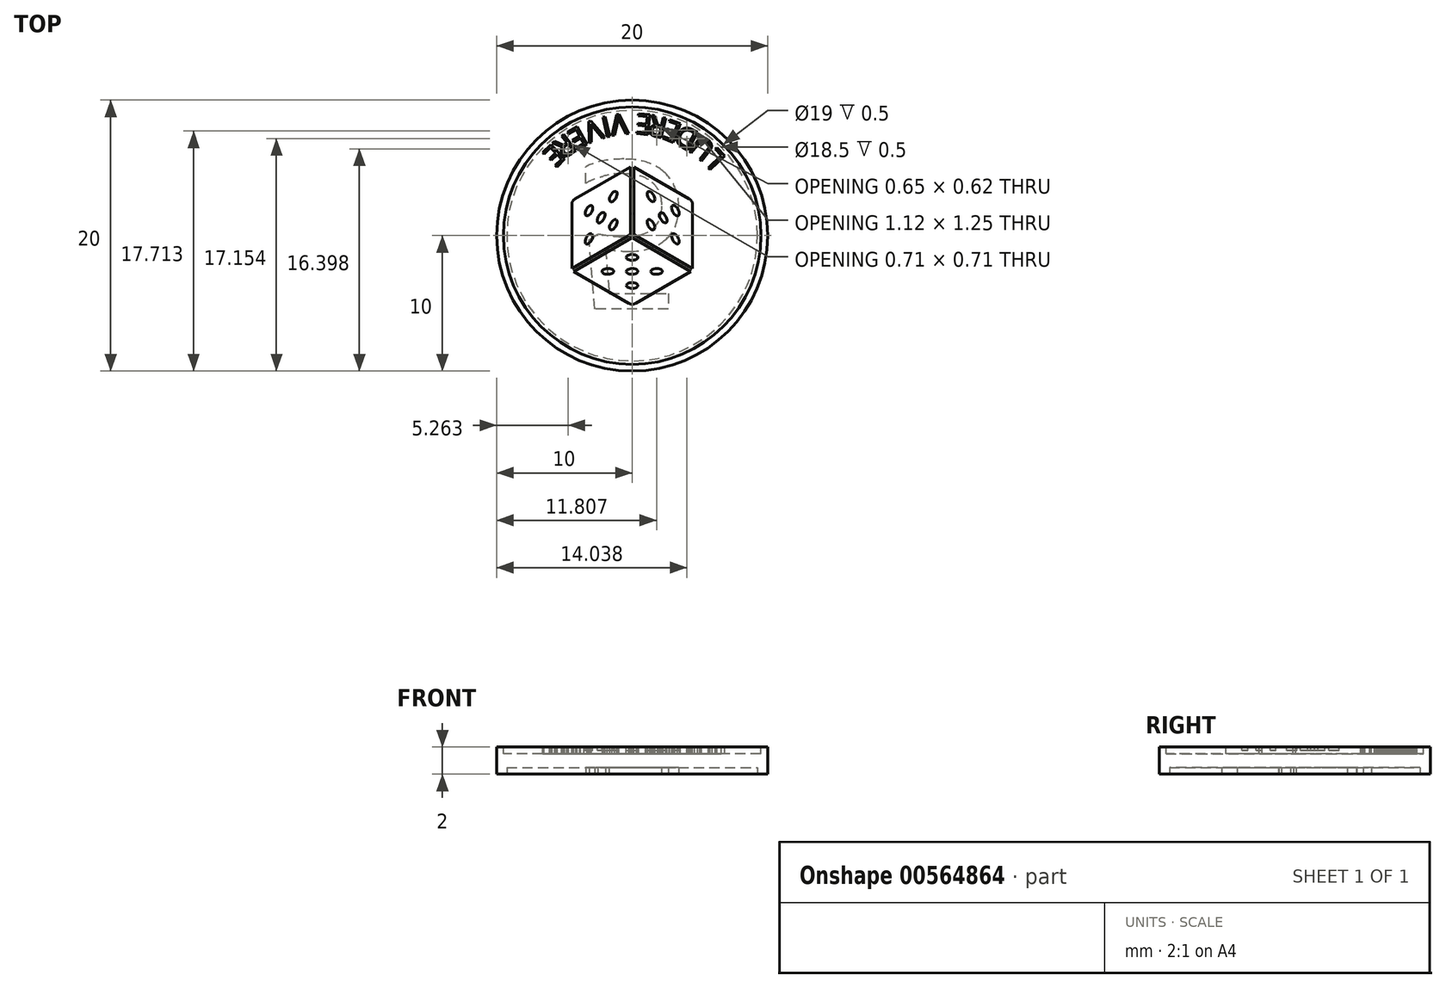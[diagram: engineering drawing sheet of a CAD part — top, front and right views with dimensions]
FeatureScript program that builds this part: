
annotation { "Feature Type Name" : "Feature", "Feature Type Description" : "" }
export const myFeature = defineFeature(function(context is Context, id is Id, definition is map)
    precondition{}
    {
        {
            var Q0;
            Q0=qCreatedBy(makeId("Top.planeOp"),FACE);
            var sketch = newSketch(context, id + "F0", { "sketchPlane" : qUnion([Q0])});
            skCircle(sketch, "E0", {"center": v(0, 0) * mm, "radius": 10 * mm});
            skSolve(sketch);
        }
        {
            var Q0;
            Q0=qSketchRegion(id+"F0",true);
            extrude(context, id + "F1", {"entities" : qUnion([Q0]), "depth" : 2 * mm});
        }
        {
            var Q0;
            Q0=makeQuery(id+"F1.opExtrude","CAP_FACE",FACE,{"disambiguationData":[OSD([sQuery(id+"F0.wireOp",EDGE,"E0")])],"isStart":false});
            var sketch = newSketch(context, id + "F2", { "sketchPlane" : qUnion([Q0])});
            skCircle(sketch, "E1.0", {"center": v(0, 0) * mm, "radius": 9.5 * mm});
            skSolve(sketch);
        }
        {
            var Q0;
            Q0=qSketchRegion(id+"F2",true);
            extrude(context, id + "F3", {"entities" : qUnion([Q0]), "operationType" : NewBodyOperationType.REMOVE, "oppositeDirection" : true, "depth" : 0.5 * mm});
        }
        {
            var Q0;
            Q0=makeQuery(id+"F1.opExtrude","CAP_FACE",FACE,{"disambiguationData":[OSD([sQuery(id+"F0.wireOp",EDGE,"E0")])],"isStart":true});
            var sketch = newSketch(context, id + "F4", { "sketchPlane" : qUnion([Q0])});
            skCircle(sketch, "E2.0", {"center": v(0, 0) * mm, "radius": 9.25 * mm});
            skSolve(sketch);
        }
        {
            var Q0;
            Q0=qSketchRegion(id+"F4",true);
            extrude(context, id + "F5", {"entities" : qUnion([Q0]), "operationType" : NewBodyOperationType.REMOVE, "oppositeDirection" : true, "depth" : 0.5 * mm});
        }
        {
            var Q0;
            Q0=makeQuery(id+"F2.imprint","IMPRINT",FACE,{"disambiguationData":[TD([[makeQuery(id+"F2.imprint","IMPRINT",EDGE,{"derivedFrom":sQuery(id+"F2.wireOp",EDGE,"E1.0")}),1.0]])]});
            var sketch = newSketch(context, id + "F6", { "sketchPlane" : qUnion([Q0])});
            skLineSegment(sketch, "E3", {"start": v(0, 0) * mm, "end": v(0, 9.5) * mm, "construction": true});
            skLineSegment(sketch, "E4", {"start": v(0, 0) * mm, "end": v(-8.23, -4.75) * mm, "construction": true});
            skLineSegment(sketch, "E5", {"start": v(0, 0) * mm, "end": v(8.23, -4.75) * mm, "construction": true});
            skCircle(sketch, "E6", {"center": v(0, 0) * mm, "radius": 9.5 * mm, "construction": true});
            skLineSegment(sketch, "E7", {"start": v(-0.13, 5.07) * mm, "end": v(-0.12, 0.07) * mm});
            skLineSegment(sketch, "E8", {"start": v(-0.12, 0.07) * mm, "end": v(-4.46, -2.43) * mm});
            skLineSegment(sketch, "E9", {"start": v(-4.46, -2.43) * mm, "end": v(-4.46, 2.28) * mm});
            skLineSegment(sketch, "E10", {"start": v(-4.2, 2.72) * mm, "end": v(-0.13, 5.07) * mm});
            skPoint(sketch, "E11.visualSharp", {"position": v(-4.46, 2.57) * mm});
            skArc(sketch, "E11.filletArc", {"start": v(-4.2, 2.72) * mm, "mid": v(-4.39, 2.53) * mm, "end": v(-4.46, 2.28) * mm});
            skPoint(sketch, "E12.1.1", {"position": v(0, -5.14) * mm});
            skLineSegment(sketch, "E12.1.3", {"start": v(-4.33, -2.64) * mm, "end": v(0, -0.14) * mm});
            skLineSegment(sketch, "E12.1.5", {"start": v(0, -0.14) * mm, "end": v(4.33, -2.64) * mm});
            skLineSegment(sketch, "E12.1.6", {"start": v(4.33, -2.64) * mm, "end": v(0.25, -5) * mm});
            skLineSegment(sketch, "E12.1.7", {"start": v(-0.25, -5) * mm, "end": v(-4.33, -2.64) * mm});
            skArc(sketch, "E12.1.8", {"start": v(-0.25, -5) * mm, "mid": v(0, -5.07) * mm, "end": v(0.25, -5) * mm});
            skPoint(sketch, "E12.2.1", {"position": v(4.46, 2.57) * mm});
            skLineSegment(sketch, "E12.2.3", {"start": v(4.46, -2.43) * mm, "end": v(0.13, 0.07) * mm});
            skLineSegment(sketch, "E12.2.5", {"start": v(0.12, 0.07) * mm, "end": v(0.13, 5.07) * mm});
            skLineSegment(sketch, "E12.2.6", {"start": v(0.13, 5.07) * mm, "end": v(4.2, 2.72) * mm});
            skLineSegment(sketch, "E12.2.7", {"start": v(4.46, 2.28) * mm, "end": v(4.46, -2.43) * mm});
            skArc(sketch, "E12.2.8", {"start": v(4.46, 2.28) * mm, "mid": v(4.39, 2.53) * mm, "end": v(4.2, 2.72) * mm});
            skSolve(sketch);
        }
        {
            var Q0;
            Q0=qSketchRegion(id+"F6",true);
            extrude(context, id + "F7", {"entities" : qUnion([Q0]), "operationType" : NewBodyOperationType.ADD, "endBound" : BoundingType.UP_TO_NEXT, "oppositeDirection" : true, "depth" : 25 * mm});
        }
        {
            var Q0;
            Q0=makeQuery(id+"F7.opExtrude","CAP_FACE",FACE,{"disambiguationData":[OSD([sQuery(id+"F6.wireOp",EDGE,"E12.1.3"),sQuery(id+"F6.wireOp",EDGE,"E12.1.5"),sQuery(id+"F6.wireOp",EDGE,"E12.1.6"),sQuery(id+"F6.wireOp",EDGE,"E12.1.7"),sQuery(id+"F6.wireOp",EDGE,"E12.1.8")])],"isStart":true});
            var sketch = newSketch(context, id + "F8", { "sketchPlane" : qUnion([Q0])});
            skLineSegment(sketch, "E13", {"start": v(-4.33, -2.64) * mm, "end": v(4.33, -2.64) * mm, "construction": true});
            skLineSegment(sketch, "E14", {"start": v(0, -0.14) * mm, "end": v(0, -5.07) * mm, "construction": true});
            skLineSegment(sketch, "E15", {"start": v(-0.56, -2.64) * mm, "end": v(0, -2.32) * mm, "construction": true});
            skLineSegment(sketch, "E16", {"start": v(0, -2.32) * mm, "end": v(0.56, -2.64) * mm, "construction": true});
            skLineSegment(sketch, "E17", {"start": v(0.56, -2.64) * mm, "end": v(0, -2.97) * mm, "construction": true});
            skLineSegment(sketch, "E18", {"start": v(0, -2.97) * mm, "end": v(-0.56, -2.64) * mm, "construction": true});
            skLineSegment(sketch, "E19", {"start": v(-0.28, -2.48) * mm, "end": v(0.28, -2.8) * mm, "construction": true});
            skLineSegment(sketch, "E20", {"start": v(-0.28, -2.8) * mm, "end": v(0.28, -2.48) * mm, "construction": true});
            skEllipse(sketch, "E21", {"center": v(0, -2.64) * mm, "majorRadius": 0.43 * mm, "minorRadius": 0.22 * mm, "majorAxis": v(-1, 0)});
            skEllipse(sketch, "E22.1.0.0", {"center": v(1.8, -2.64) * mm, "majorRadius": 0.43 * mm, "minorRadius": 0.22 * mm, "majorAxis": v(-1, 0)});
            skLineSegment(sketch, "E22.direction1", {"start": v(0, -2.64) * mm, "end": v(1.8, -2.64) * mm, "construction": true});
            skEllipse(sketch, "E23.1.0.0", {"center": v(-1.8, -2.64) * mm, "majorRadius": 0.43 * mm, "minorRadius": 0.22 * mm, "majorAxis": v(-1, 0)});
            skLineSegment(sketch, "E23.direction1", {"start": v(0, -2.64) * mm, "end": v(-1.8, -2.64) * mm, "construction": true});
            skEllipse(sketch, "E24.1.0.0", {"center": v(0, -3.68) * mm, "majorRadius": 0.43 * mm, "minorRadius": 0.22 * mm, "majorAxis": v(-1, 0)});
            skLineSegment(sketch, "E24.direction1", {"start": v(0, -2.64) * mm, "end": v(0, -3.68) * mm, "construction": true});
            skLineSegment(sketch, "E25", {"start": v(0, -3.68) * mm, "end": v(1.8, -2.64) * mm, "construction": true});
            skEllipse(sketch, "E26.1.0.0", {"center": v(0, -1.6) * mm, "majorRadius": 0.43 * mm, "minorRadius": 0.22 * mm, "majorAxis": v(-1, 0)});
            skLineSegment(sketch, "E26.direction1", {"start": v(0, -2.64) * mm, "end": v(0, -1.6) * mm, "construction": true});
            skLineSegment(sketch, "E27", {"start": v(-1.8, -2.64) * mm, "end": v(0, -1.6) * mm});
            skLineSegment(sketch, "E28.1.0", {"start": v(2.3, 1.32) * mm, "end": v(3.2, -0.24) * mm, "construction": true});
            skLineSegment(sketch, "E28.1.1", {"start": v(3.2, -0.24) * mm, "end": v(1.4, 0.8) * mm});
            skEllipse(sketch, "E28.1.2", {"center": v(1.4, 0.8) * mm, "majorRadius": 0.43 * mm, "minorRadius": 0.22 * mm, "majorAxis": v(0.5, -0.87)});
            skEllipse(sketch, "E28.1.3", {"center": v(1.4, 2.88) * mm, "majorRadius": 0.43 * mm, "minorRadius": 0.22 * mm, "majorAxis": v(0.5, -0.87)});
            skLineSegment(sketch, "E28.1.4", {"start": v(2.3, 1.32) * mm, "end": v(1.4, 2.88) * mm, "construction": true});
            skEllipse(sketch, "E28.1.5", {"center": v(3.2, -0.24) * mm, "majorRadius": 0.43 * mm, "minorRadius": 0.22 * mm, "majorAxis": v(0.5, -0.87)});
            skLineSegment(sketch, "E28.1.6", {"start": v(2.3, 1.32) * mm, "end": v(1.4, 0.8) * mm, "construction": true});
            skEllipse(sketch, "E28.1.7", {"center": v(3.2, 1.84) * mm, "majorRadius": 0.43 * mm, "minorRadius": 0.22 * mm, "majorAxis": v(0.5, -0.87)});
            skLineSegment(sketch, "E28.1.8", {"start": v(4.46, -2.43) * mm, "end": v(0.12, 5.07) * mm, "construction": true});
            skLineSegment(sketch, "E28.1.9", {"start": v(0.12, 0.07) * mm, "end": v(4.39, 2.53) * mm, "construction": true});
            skLineSegment(sketch, "E28.1.10", {"start": v(3.2, 1.84) * mm, "end": v(1.4, 2.88) * mm, "construction": true});
            skLineSegment(sketch, "E28.1.11", {"start": v(2.3, 1.32) * mm, "end": v(3.2, 1.84) * mm, "construction": true});
            skEllipse(sketch, "E28.1.12", {"center": v(2.3, 1.32) * mm, "majorRadius": 0.43 * mm, "minorRadius": 0.22 * mm, "majorAxis": v(0.5, -0.87)});
            skLineSegment(sketch, "E28.1.13", {"start": v(2.57, 1.16) * mm, "end": v(2, 1.48) * mm, "construction": true});
            skLineSegment(sketch, "E28.1.14", {"start": v(2.3, 1) * mm, "end": v(2.3, 1.65) * mm, "construction": true});
            skLineSegment(sketch, "E28.1.15", {"start": v(2, 1.8) * mm, "end": v(2.57, 1.48) * mm, "construction": true});
            skLineSegment(sketch, "E28.1.16", {"start": v(2.57, 1.48) * mm, "end": v(2.57, 0.83) * mm, "construction": true});
            skLineSegment(sketch, "E28.1.17", {"start": v(2, 1.16) * mm, "end": v(2, 1.8) * mm, "construction": true});
            skLineSegment(sketch, "E28.1.18", {"start": v(2.57, 0.83) * mm, "end": v(2, 1.16) * mm, "construction": true});
            skLineSegment(sketch, "E28.2.0", {"start": v(-2.3, 1.32) * mm, "end": v(-1.4, 2.88) * mm, "construction": true});
            skLineSegment(sketch, "E28.2.1", {"start": v(-1.4, 2.88) * mm, "end": v(-1.4, 0.8) * mm});
            skEllipse(sketch, "E28.2.2", {"center": v(-1.4, 0.8) * mm, "majorRadius": 0.43 * mm, "minorRadius": 0.22 * mm, "majorAxis": v(0.5, 0.87)});
            skEllipse(sketch, "E28.2.3", {"center": v(-3.2, -0.24) * mm, "majorRadius": 0.43 * mm, "minorRadius": 0.22 * mm, "majorAxis": v(0.5, 0.87)});
            skLineSegment(sketch, "E28.2.4", {"start": v(-2.3, 1.32) * mm, "end": v(-3.2, -0.24) * mm, "construction": true});
            skEllipse(sketch, "E28.2.5", {"center": v(-1.4, 2.88) * mm, "majorRadius": 0.43 * mm, "minorRadius": 0.22 * mm, "majorAxis": v(0.5, 0.87)});
            skLineSegment(sketch, "E28.2.6", {"start": v(-2.3, 1.32) * mm, "end": v(-1.4, 0.8) * mm, "construction": true});
            skEllipse(sketch, "E28.2.7", {"center": v(-3.2, 1.84) * mm, "majorRadius": 0.43 * mm, "minorRadius": 0.22 * mm, "majorAxis": v(0.5, 0.87)});
            skLineSegment(sketch, "E28.2.8", {"start": v(-0.12, 5.07) * mm, "end": v(-4.46, -2.43) * mm, "construction": true});
            skLineSegment(sketch, "E28.2.9", {"start": v(-0.12, 0.07) * mm, "end": v(-4.39, 2.53) * mm, "construction": true});
            skLineSegment(sketch, "E28.2.10", {"start": v(-3.2, 1.84) * mm, "end": v(-3.2, -0.24) * mm, "construction": true});
            skLineSegment(sketch, "E28.2.11", {"start": v(-2.3, 1.32) * mm, "end": v(-3.2, 1.84) * mm, "construction": true});
            skEllipse(sketch, "E28.2.12", {"center": v(-2.3, 1.32) * mm, "majorRadius": 0.43 * mm, "minorRadius": 0.22 * mm, "majorAxis": v(0.5, 0.87)});
            skLineSegment(sketch, "E28.2.13", {"start": v(-2.3, 1.65) * mm, "end": v(-2.3, 1) * mm, "construction": true});
            skLineSegment(sketch, "E28.2.14", {"start": v(-2, 1.48) * mm, "end": v(-2.57, 1.16) * mm, "construction": true});
            skLineSegment(sketch, "E28.2.15", {"start": v(-2.57, 0.83) * mm, "end": v(-2.57, 1.48) * mm, "construction": true});
            skLineSegment(sketch, "E28.2.16", {"start": v(-2.57, 1.48) * mm, "end": v(-2, 1.8) * mm, "construction": true});
            skLineSegment(sketch, "E28.2.17", {"start": v(-2, 1.16) * mm, "end": v(-2.57, 0.83) * mm, "construction": true});
            skLineSegment(sketch, "E28.2.18", {"start": v(-2, 1.8) * mm, "end": v(-2, 1.16) * mm, "construction": true});
            skPoint(sketch, "E28.center", {"position": v(0, 0) * mm});
            skCircle(sketch, "E29", {"center": v(0, 0) * mm, "radius": 9 * mm, "construction": true});
            skSolve(sketch);
        }
        {
            var Q0;
            Q0=qSketchRegion(id+"F8",true);
            extrude(context, id + "F9", {"entities" : qUnion([Q0]), "operationType" : NewBodyOperationType.REMOVE, "oppositeDirection" : true, "depth" : 0.25 * mm});
        }
        {
            var Q0;
            Q0=makeQuery(id+"F7.opExtrude","CAP_FACE",FACE,{"disambiguationData":[OSD([sQuery(id+"F6.wireOp",EDGE,"E12.2.3"),sQuery(id+"F6.wireOp",EDGE,"E12.2.5"),sQuery(id+"F6.wireOp",EDGE,"E12.2.6"),sQuery(id+"F6.wireOp",EDGE,"E12.2.7"),sQuery(id+"F6.wireOp",EDGE,"E12.2.8")])],"isStart":true});
            var sketch = newSketch(context, id + "F10", { "sketchPlane" : qUnion([Q0])});
            skCircle(sketch, "E30", {"center": v(0, 0) * mm, "radius": 9 * mm, "construction": true});
            skLineSegment(sketch, "E31", {"start": v(0, 0) * mm, "end": v(0.12, 9) * mm, "construction": true});
            skText(sketch, "E32", { "text": "E", "fontName": "OpenSans-Regular.ttf"});
            skText(sketch, "E33", { "text": "L", "fontName": "OpenSans-Regular.ttf"});
            skText(sketch, "E34", { "text": "U", "fontName": "OpenSans-Regular.ttf"});
            skText(sketch, "E35", { "text": "D", "fontName": "OpenSans-Regular.ttf"});
            skText(sketch, "E36", { "text": "E", "fontName": "OpenSans-Regular.ttf"});
            skText(sketch, "E37", { "text": "R", "fontName": "OpenSans-Regular.ttf"});
            skText(sketch, "E38", { "text": "V", "fontName": "OpenSans-Regular.ttf"});
            skText(sketch, "E39", { "text": "I", "fontName": "OpenSans-Regular.ttf"});
            skText(sketch, "E40", { "text": "V", "fontName": "OpenSans-Regular.ttf"});
            skText(sketch, "E41", { "text": "E", "fontName": "OpenSans-Regular.ttf"});
            skText(sketch, "E42", { "text": "R", "fontName": "OpenSans-Regular.ttf"});
            skText(sketch, "E43", { "text": "E", "fontName": "OpenSans-Regular.ttf"});
            const initialGuessF10  = {"E32": [0.0015, 0.0089, -0.99489, 0.10098, 0.0015], "E33": [0.00696, 0.00574, -0.6846, 0.72892, 0.0015], "E34": [0.0062, 0.00656, -0.77938, 0.62655, 0.0015], "E35": [0.005, 0.00752, -0.87634, 0.48169, 0.0015], "E36": [0.00374, 0.0082, -0.93485, 0.35504, 0.0015], "E37": [0.00267, 0.00862, -0.97517, 0.22148, 0.0015], "E38": [-0.00045, 0.00902, -0.9921, -0.1254, 0.0015], "E39": [-0.0018, 0.00882, -0.97356, -0.22842, 0.0015], "E40": [-0.00254, 0.00866, -0.93542, -0.35354, 0.0015], "E41": [-0.00388, 0.00814, -0.87289, -0.48792, 0.0015], "E42": [-0.00489, 0.00759, -0.79649, -0.60466, 0.0015], "E43": [-0.00586, 0.00686, -0.71686, -0.69722, 0.0015]};
            skSetInitialGuess(sketch, initialGuessF10);
            skSolve(sketch);
        }
        {
            var Q0;
            Q0=qSketchRegion(id+"F10",true);
            var Q1;
            Q1=makeQuery(id+"F7.opExtrude","CAP_FACE",FACE,{"disambiguationData":[OSD([sQuery(id+"F6.wireOp",EDGE,"E12.2.3"),sQuery(id+"F6.wireOp",EDGE,"E12.2.5"),sQuery(id+"F6.wireOp",EDGE,"E12.2.6"),sQuery(id+"F6.wireOp",EDGE,"E12.2.7"),sQuery(id+"F6.wireOp",EDGE,"E12.2.8")])],"isStart":true});
            extrude(context, id + "F11", {"entities" : qUnion([Q0]), "endBound" : BoundingType.UP_TO_NEXT, "oppositeDirection" : true, "endBoundEntityFace" : qUnion([Q1]), "depth" : 25 * mm});
        }
        {
            var Q0;
            Q0=makeQuery(id+"F4.imprint","IMPRINT",FACE,{"disambiguationData":[TD([[makeQuery(id+"F4.imprint","IMPRINT",EDGE,{"derivedFrom":sQuery(id+"F4.wireOp",EDGE,"E2.0")}),-1.0]])]});
            cPlane(context, id + "F12", {"entities" : qUnion([Q0]), "cplaneType" : CPlaneType.OFFSET, "offset" : 0 * mm, "width" : 150 * mm, "height" : 150 * mm});
        }
        {
            var Q0;
            Q0=qCreatedBy(id+"F12.planeOp",FACE);
            var sketch = newSketch(context, id + "F13", { "sketchPlane" : qUnion([Q0])});
            skText(sketch, "E44", { "text": "5", "fontName": "OpenSans-Regular.ttf"});
            skPoint(sketch, "E45", {"position": v(0, 0) * mm});
            const initialGuessF13  = {"E44": [-0.00442, -0.0055, 1, 0, 0.011]};
            skSetInitialGuess(sketch, initialGuessF13);
            skSolve(sketch);
        }
        {
            var Q0;
            Q0=qSketchRegion(id+"F13",true);
            extrude(context, id + "F14", {"entities" : qUnion([Q0]), "endBound" : BoundingType.UP_TO_NEXT, "oppositeDirection" : true, "depth" : 25 * mm});
        }
    });
